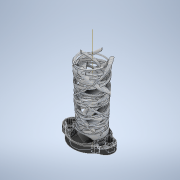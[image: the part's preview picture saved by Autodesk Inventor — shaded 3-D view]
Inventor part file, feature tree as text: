
AUTODESK INVENTOR PART (.ipt)
format: ipt  version: 2022 (Build 260153000, 153)  size: 7,142,400 bytes
history: native  units: mm
features: sketch x24, fillet x22, helix x12, extrude x10, other x2, revolve x2, imported_body x1
ambient origin geometry x8: Origin, YZ Plane, XZ Plane, XY Plane, X Axis, Y Axis, Z Axis, Center Point
bodies: Body1 (feature_tree), Body2 (feature_tree)
feature tree (73):
  imported_body  "Base"
  extrude  "Extrusion1"  Depth=70.0mm
  extrude  "Extrusion6"  Depth=70.0mm
  extrude  "Extrusion7"  Depth=72.0mm
  extrude  "Extrusion8"  Depth=3.0mm
  fillet  "Fillet5"  Radius=10.0mm
  extrude  "Extrusion9"  Depth=15.0mm
  extrude  "Extrusion10"  Depth=90.0mm
  fillet  "Fillet6"  Radius=20.0mm
  fillet  "Fillet10"  Radius=25.0mm
  fillet  "Fillet11"  Radius=30.0mm
  fillet  "Fillet12"  Radius=9.0mm
  fillet  "Fillet13"  Radius=60.0mm
  fillet  "Fillet14"  Radius=30.0mm
  extrude  "Extrusion11"  Depth=7.0mm
  extrude  "Extrusion12"  Depth=90.0mm
  other  "Work Axis1"
  revolve  "Revolution1"  [1 undecoded]
  extrude  "Extrusion13"  Depth=18.0mm
  helix  "Coil1"  [1 undecoded]
  helix  "Coil2"  [1 undecoded]
  helix  "Coil3"  [1 undecoded]
  helix  "Coil4"  [1 undecoded]
  helix  "Coil5"  [1 undecoded]
  helix  "Coil6"  [1 undecoded]
  helix  "Coil7"  [1 undecoded]
  helix  "Coil9"  [1 undecoded]
  helix  "Coil10"  [1 undecoded]
  helix  "Coil11"  [1 undecoded]
  helix  "Coil12"  [1 undecoded]
  helix  "Coil13"  [1 undecoded]
  extrude  "Extrusion14"  Depth=15.0mm
  fillet  "Fillet17"  Radius=75.0mm
  fillet  "Fillet18"  Radius=100.0mm
  fillet  "Fillet19"  Radius=30.0mm
  fillet  "Fillet20"  Radius=5.0mm
  fillet  "Fillet21"  Radius=2.0mm
  fillet  "Fillet22"  Radius=5.0mm
  fillet  "Fillet23"  Radius=5.0mm
  fillet  "Fillet24"  Radius=5.0mm
  fillet  "Fillet25"  [1 undecoded]
  fillet  "Fillet26"  Radius=2.5mm
  fillet  "Fillet27"  Radius=100.0mm
  fillet  "Fillet28"  Radius=2.5mm
  fillet  "Fillet29"  [1 undecoded]
  fillet  "Fillet30"  Radius=50.0mm
  fillet  "Fillet31"  Radius=3.0mm
  revolve  "Revolution2"  Angle=240.0deg
  sketch  "Sketch1"  dims[d4=28.0mm d5=0.0mm d79=70.0mm]
  sketch  "Sketch6"  dims[d80=80.0mm]
  sketch  "Sketch7"  dims[d87=24.0mm d88=25.0mm d89=22.5mm d90=26.0mm d91=18.0mm d92=18.0mm d94=9.0mm d95=21.5mm d96=21.5mm d97=10.75mm d98=10.75mm d99=25.0mm d100=70.0mm]
  sketch  "Sketch8"  dims[d101=70.0mm d102=72.0mm]
  sketch  "Sketch9"  dims[d103=72.0mm d104=3.0mm d105=10.0mm d106=0.0mm]
  sketch  "Sketch11"  dims[d107=100.0mm d108=15.0mm]
  sketch  "Sketch12"  dims[d109=25.0mm d110=0.0mm d111=90.0mm d112=20.0mm d113=25.0mm d114=0.0mm d115=30.0mm d116=9.0mm d117=60.0mm d118=30.0mm]
  sketch  "Sketch13"  dims[d119=62.0mm d120=7.0mm]
  other  "Tower"
  sketch  "Sketch14"  dims[d121=4.0mm d122=90.0mm]
  sketch  "Sketch15"  dims[d123=24.0mm d124=67.0mm]
  sketch  "Sketch16"  dims[d125=65.0mm d126=18.0mm d127=3.0mm d128=90.0mm d129=24.0mm d130=66.0mm d131=50.0mm d132=50.0mm d133=77.0mm d134=55.0mm d135=55.0mm d136=80.0mm d137=69.0mm d138=25.0mm d139=0.0mm]
  sketch  "Sketch17"  dims[d140=15.0mm d141=15.0mm d142=75.0mm d143=100.0mm d144=-0.349066mm d145=30.0mm d149=5.0mm d150=2.0mm d151=5.0mm d152=5.0mm d153=5.0mm d154=0.0mm d155=2.5mm d156=100.0mm d157=0.0mm d160=2.5mm d161=0.0mm d162=50.0mm d163=0.0mm d164=3.0mm]
  sketch  "Sketch18"  dims[d166=0.0mm d167=240.0deg]
  sketch  "Sketch19"  dims[d168=0.0mm]
  sketch  "Sketch20"  dims[d176=40.0mm d177=0.0mm]
  sketch  "Sketch21"  dims[d181=10.0mm]
  sketch  "Sketch22"  dims[d182=10.0mm]
  sketch  "Sketch23"  dims[d183=20.0mm]
  sketch  "Sketch24"  dims[d186=40.0mm]
  sketch  "Sketch25"  dims[d188=9.0mm]
  sketch  "Sketch26"  dims[d199=41.0mm d200=250.0mm d201=100.0mm d202=0.349066mm d203=90.0deg d204=90.0deg d205=0.0mm d206=0.0mm d207=5.0mm]
  sketch  "Sketch27"  dims[d208=7.0mm]
  sketch  "Sketch28"  dims[d209=43.0mm]
  sketch  "Sketch29"  dims[d210=14.0mm d211=9.0mm d220=277.0mm d221=260.0mm d222=13.5mm d223=0.244346mm d224=90.0deg d225=90.0deg d226=0.0mm d227=0.0mm d228=20.0mm d229=11.0mm d230=13.0mm d231=307.0mm d232=250.0mm d233=13.5mm d234=0.523599mm d235=90.0deg d236=90.0deg d237=0.0mm d238=0.0mm d239=25.0mm d240=13.0mm d241=14.5mm d242=313.0mm d243=250.0mm d244=13.5mm d245=0.523599mm d246=90.0deg d247=90.0deg d248=0.0mm d249=0.0mm d250=7.0mm d251=10.0mm d252=10.0mm d253=11.0mm d254=353.0mm d255=270.0mm d256=13.5mm d257=0.349066mm d258=90.0deg d259=90.0deg d260=0.0mm d261=0.0mm d262=8.0mm d263=5.0mm d264=8.0mm d265=40.0mm d266=317.0mm d267=270.0mm d268=13.5mm d269=0.698132mm d270=90.0deg d271=90.0deg d272=0.0mm d273=0.0mm d274=6.0mm d275=5.0mm d276=5.5mm d277=37.0mm d278=260.0mm d279=13.5mm d280=0.418879mm d281=90.0deg d282=90.0deg d283=0.0mm d284=0.0mm d285=9.0mm d286=4.5mm d287=48.0mm d312=71.0mm d313=240.0mm d314=13.5mm d315=0.303687mm d316=90.0deg d317=90.0deg d318=0.0mm d319=0.0mm d320=11.0mm d321=5.5mm d322=5.7mm d323=59.0mm d324=240.0mm d325=13.5mm d326=0.471239mm d327=90.0deg d328=90.0deg d329=0.0mm d330=0.0mm d331=6.0mm d332=3.2mm d333=8.0mm d334=3.8mm d335=271.0mm d336=260.0mm d337=13.5mm d338=0.401426mm d339=90.0deg d340=90.0deg d341=0.0mm d342=0.0mm d351=109.0mm d352=270.0mm d353=13.5mm d354=-0.122173mm d355=90.0deg d356=90.0deg d357=0.0mm d358=0.0mm d359=109.0mm d360=270.0mm d361=13.5mm d362=-0.122173mm d363=90.0deg d364=90.0deg d365=0.0mm d366=0.0mm d367=10.0mm d368=0.0mm d369=2.0mm d370=2.0mm d371=2.0mm d372=2.0mm d373=2.0mm d374=2.0mm d375=2.0mm d376=2.0mm d377=4.0mm d378=2.0mm d379=2.0mm d380=2.0mm d381=2.0mm d382=4.0mm d383=2.0mm d384=17.453293mm]
note: 15 required parameter values undecoded (feature->parameter linkage not recoverable at this tier; creation-order binding heuristic only, values carry confidence <= 0.55)